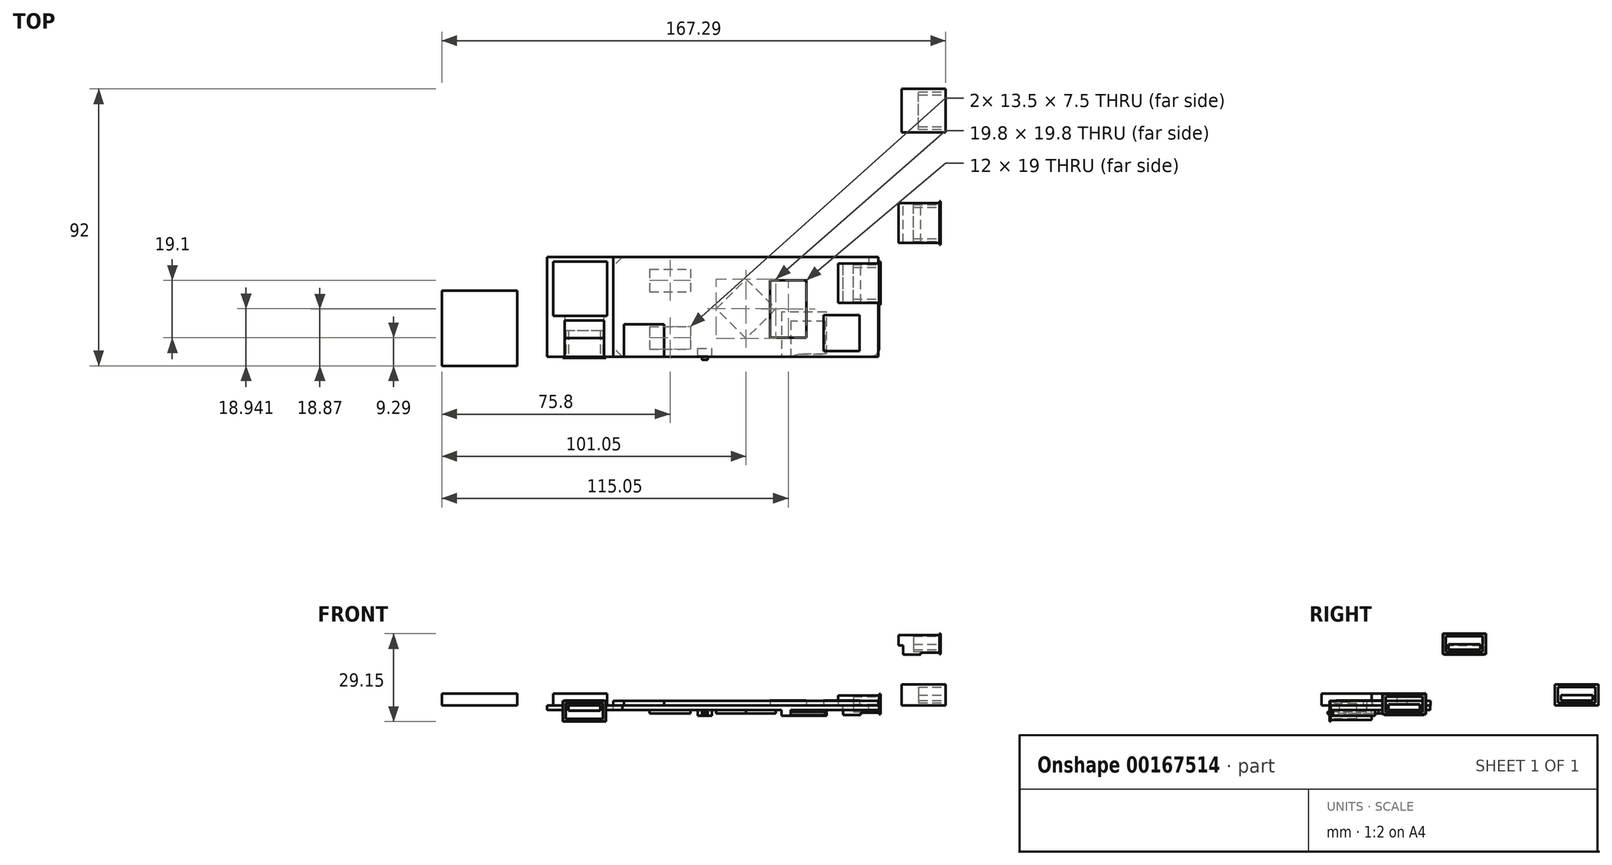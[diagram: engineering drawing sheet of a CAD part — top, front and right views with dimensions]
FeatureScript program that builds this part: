
annotation { "Feature Type Name" : "Feature", "Feature Type Description" : "" }
export const myFeature = defineFeature(function(context is Context, id is Id, definition is map)
    precondition{}
    {
        {
            var Q0;
            Q0=qCreatedBy(makeId("Top.planeOp"),FACE);
            var sketch = newSketch(context, id + "F0", { "sketchPlane" : qUnion([Q0])});
            skLineSegment(sketch, "E0", {"start": v(0, 0) * mm, "end": v(88.3, 0) * mm, "construction": true});
            skLineSegment(sketch, "E1", {"start": v(0, 0) * mm, "end": v(0, 13.55) * mm});
            skLineSegment(sketch, "E2", {"start": v(3, 16.55) * mm, "end": v(84.8, 16.55) * mm});
            skLineSegment(sketch, "E3", {"start": v(88.3, 1.25) * mm, "end": v(88.3, 0) * mm});
            skLineSegment(sketch, "E4", {"start": v(3, 16.55) * mm, "end": v(0, 13.55) * mm});
            skLineSegment(sketch, "E5.0.MirrorCS", {"start": v(0, 0) * mm, "end": v(0, -13.55) * mm});
            skLineSegment(sketch, "E6.0.MirrorCS", {"start": v(3, -16.55) * mm, "end": v(0, -13.55) * mm});
            skLineSegment(sketch, "E7.0.MirrorCS", {"start": v(3, -16.55) * mm, "end": v(85.3, -16.55) * mm});
            skArc(sketch, "E8.0.MirrorCS", {"start": v(88.3, -13.55) * mm, "mid": v(87.42, -15.67) * mm, "end": v(85.3, -16.55) * mm});
            skLineSegment(sketch, "E9.0.MirrorCS", {"start": v(88.3, -13.55) * mm, "end": v(88.3, 0) * mm});
            skLineSegment(sketch, "E10", {"start": v(84.8, 16.55) * mm, "end": v(84.8, 14.45) * mm});
            skLineSegment(sketch, "E11", {"start": v(84.8, 14.45) * mm, "end": v(76.2, 14.45) * mm});
            skLineSegment(sketch, "E12", {"start": v(76.2, 14.45) * mm, "end": v(76.2, 1.25) * mm});
            skLineSegment(sketch, "E13", {"start": v(76.2, 1.25) * mm, "end": v(88.3, 1.25) * mm});
            skLineSegment(sketch, "E14.bottom", {"start": v(52.1, 8.78) * mm, "end": v(64.1, 8.78) * mm});
            skLineSegment(sketch, "E14.top", {"start": v(52.1, -10.22) * mm, "end": v(64.1, -10.22) * mm});
            skLineSegment(sketch, "E14.left", {"start": v(52.1, 8.78) * mm, "end": v(52.1, -10.22) * mm});
            skLineSegment(sketch, "E14.right", {"start": v(64.1, 8.78) * mm, "end": v(64.1, -10.22) * mm});
            skLineSegment(sketch, "E15.bottom", {"start": v(69.8, -2.75) * mm, "end": v(81.8, -2.75) * mm});
            skLineSegment(sketch, "E15.top", {"start": v(69.8, -14.75) * mm, "end": v(81.8, -14.75) * mm});
            skLineSegment(sketch, "E15.left", {"start": v(69.8, -2.75) * mm, "end": v(69.8, -14.75) * mm});
            skLineSegment(sketch, "E15.right", {"start": v(81.8, -2.75) * mm, "end": v(81.8, -14.75) * mm});
            skLineSegment(sketch, "E16.bottom", {"start": v(12.1, 12.55) * mm, "end": v(25.6, 12.55) * mm});
            skLineSegment(sketch, "E16.top", {"start": v(12.1, 5.05) * mm, "end": v(25.6, 5.05) * mm});
            skLineSegment(sketch, "E16.left", {"start": v(12.1, 12.55) * mm, "end": v(12.1, 5.05) * mm});
            skLineSegment(sketch, "E16.right", {"start": v(25.6, 12.55) * mm, "end": v(25.6, 5.05) * mm});
            skLineSegment(sketch, "E17.bottom", {"start": v(12.1, -6.55) * mm, "end": v(25.6, -6.55) * mm});
            skLineSegment(sketch, "E17.top", {"start": v(12.1, -14.05) * mm, "end": v(25.6, -14.05) * mm});
            skLineSegment(sketch, "E17.left", {"start": v(12.1, -6.55) * mm, "end": v(12.1, -14.05) * mm});
            skLineSegment(sketch, "E17.right", {"start": v(25.6, -6.55) * mm, "end": v(25.6, -14.05) * mm});
            skLineSegment(sketch, "E18", {"start": v(44.1, 9.25) * mm, "end": v(54, -0.65) * mm});
            skLineSegment(sketch, "E19", {"start": v(54, -0.65) * mm, "end": v(44.1, -10.55) * mm});
            skLineSegment(sketch, "E20", {"start": v(44.1, -10.55) * mm, "end": v(34.2, -0.65) * mm});
            skLineSegment(sketch, "E21", {"start": v(34.2, -0.65) * mm, "end": v(44.1, 9.25) * mm});
            skLineSegment(sketch, "E22.bottom", {"start": v(28, -16.25) * mm, "end": v(29.4, -16.25) * mm});
            skLineSegment(sketch, "E22.top", {"start": v(28, -13.75) * mm, "end": v(32.7, -13.75) * mm});
            skLineSegment(sketch, "E22.left", {"start": v(28, -16.25) * mm, "end": v(28, -13.75) * mm});
            skLineSegment(sketch, "E22.right", {"start": v(32.7, -16.25) * mm, "end": v(32.7, -13.75) * mm});
            skLineSegment(sketch, "E23", {"start": v(31.3, -16.25) * mm, "end": v(31.3, -17.55) * mm});
            skLineSegment(sketch, "E24", {"start": v(31.3, -17.55) * mm, "end": v(29.4, -17.55) * mm});
            skLineSegment(sketch, "E25", {"start": v(29.4, -17.55) * mm, "end": v(29.4, -16.25) * mm});
            skLineSegment(sketch, "E26.trimOffspring", {"start": v(31.3, -16.25) * mm, "end": v(32.7, -16.25) * mm});
            skLineSegment(sketch, "E27", {"start": v(29.4, -16.25) * mm, "end": v(31.3, -16.25) * mm});
            skLineSegment(sketch, "E28", {"start": v(70.8, -1.75) * mm, "end": v(55.9, -1.75) * mm});
            skLineSegment(sketch, "E29", {"start": v(55.9, -1.75) * mm, "end": v(55.9, -16.55) * mm});
            skLineSegment(sketch, "E30", {"start": v(55.9, -16.55) * mm, "end": v(58.9, -16.55) * mm});
            skLineSegment(sketch, "E31", {"start": v(58.9, -16.55) * mm, "end": v(61.8, -15.75) * mm});
            skLineSegment(sketch, "E32", {"start": v(61.8, -15.75) * mm, "end": v(70.8, -15.75) * mm});
            skLineSegment(sketch, "E33", {"start": v(70.8, -15.75) * mm, "end": v(70.8, -1.75) * mm});
            skSolve(sketch);
        }
        {
            var Q0;
            Q0=qCreatedBy(makeId("Top.planeOp"),FACE);
            var sketch = newSketch(context, id + "F1", { "sketchPlane" : qUnion([Q0])});
            skLineSegment(sketch, "E34", {"start": v(88.3, 1.25) * mm, "end": v(76.3, 1.25) * mm});
            skLineSegment(sketch, "E35", {"start": v(76.3, 1.25) * mm, "end": v(76.3, 14.45) * mm});
            skLineSegment(sketch, "E36", {"start": v(76.3, 14.45) * mm, "end": v(88.3, 14.45) * mm});
            skLineSegment(sketch, "E37", {"start": v(88.3, 14.45) * mm, "end": v(88.3, 1.25) * mm});
            skLineSegment(sketch, "E38", {"start": v(88.3, 14.45) * mm, "end": v(88.3, 15.05) * mm});
            skLineSegment(sketch, "E39", {"start": v(88.3, 15.05) * mm, "end": v(88.7, 15.05) * mm});
            skLineSegment(sketch, "E40", {"start": v(88.7, 15.05) * mm, "end": v(88.7, 0.65) * mm});
            skLineSegment(sketch, "E41", {"start": v(88.7, 0.65) * mm, "end": v(88.3, 0.65) * mm});
            skLineSegment(sketch, "E42", {"start": v(88.3, 0.65) * mm, "end": v(88.3, 1.25) * mm});
            skLineSegment(sketch, "E43", {"start": v(76.3, 14.45) * mm, "end": v(74.7, 14.45) * mm});
            skLineSegment(sketch, "E44", {"start": v(74.7, 14.45) * mm, "end": v(74.7, 1.25) * mm});
            skLineSegment(sketch, "E45", {"start": v(74.7, 1.25) * mm, "end": v(76.3, 1.25) * mm});
            skLineSegment(sketch, "E46", {"start": v(82.1, 1.25) * mm, "end": v(82.1, 14.45) * mm});
            skSolve(sketch);
        }
        {
            var Q0;
            Q0=makeQuery(id+"F1.imprint","IMPRINT",FACE,{"disambiguationData":[TD([[makeQuery(id+"F1.imprint","IMPRINT",EDGE,{"derivedFrom":sQuery(id+"F1.wireOp",EDGE,"E34")}),-1.0]])]});
            var Q1;
            Q1=makeQuery(id+"F1.imprint","IMPRINT",FACE,{"disambiguationData":[TD([[makeQuery(id+"F1.imprint","IMPRINT",EDGE,{"derivedFrom":sQuery(id+"F1.wireOp",EDGE,"E35")}),1.0]])]});
            extrude(context, id + "F2", {"entities" : qUnion([Q0, Q1]), "depth" : (4.8 - 1.45) * mm});
        }
        {
            var Q0;
            {var subQ2=sQuery(id+"F1.wireOp",EDGE,"E35");Q0=makeQuery(id+"F1.imprint","IMPRINT",FACE,{"disambiguationData":[TD([[makeQuery(id+"F1.imprint","IMPRINT",EDGE,{"derivedFrom":subQ2}),-1.0]])]});}
            extrude(context, id + "F3", {"entities" : qUnion([Q0]), "operationType" : NewBodyOperationType.ADD, "oppositeDirection" : true, "depth" : (6.5 - 4.8 + 1.45) * mm});
        }
        {
            var Q0;
            {var subQ1=sQuery(id+"F1.wireOp",EDGE,"E37");Q0=makeQuery(id+"F1.imprint","IMPRINT",FACE,{"disambiguationData":[TD([[makeQuery(id+"F1.imprint","IMPRINT",EDGE,{"derivedFrom":subQ1}),-1.0]])]});}
            extrude(context, id + "F4", {"entities" : qUnion([Q0]), "operationType" : NewBodyOperationType.ADD, "oppositeDirection" : true, "depth" : 2.45 * mm});
        }
        {
            var Q0;
            Q0=makeQuery(id+"F1.imprint","IMPRINT",FACE,{"disambiguationData":[TD([[makeQuery(id+"F1.imprint","IMPRINT",EDGE,{"derivedFrom":sQuery(id+"F1.wireOp",EDGE,"E37")}),1.0]])]});
            extrude(context, id + "F5", {"entities" : qUnion([Q0]), "operationType" : NewBodyOperationType.ADD, "depth" : 3.85 * mm, "hasSecondDirection" : true, "secondDirectionOppositeDirection" : true, "secondDirectionDepth" : 2.95 * mm});
        }
        {
            var Q0;
            Q0=makeQuery(id+"F5.opExtrude","SWEPT_FACE",FACE,{"disambiguationData":[OSD([sQuery(id+"F1.wireOp",EDGE,"E40")])]});
            var sketch = newSketch(context, id + "F6", { "sketchPlane" : qUnion([Q0])});
            skLineSegment(sketch, "E47.bottom", {"start": v(1.75, 3) * mm, "end": v(13.95, 3) * mm});
            skLineSegment(sketch, "E47.top", {"start": v(1.75, -2.1) * mm, "end": v(13.95, -2.1) * mm});
            skLineSegment(sketch, "E47.left", {"start": v(1.75, 3) * mm, "end": v(1.75, -2.1) * mm});
            skLineSegment(sketch, "E47.right", {"start": v(13.95, 3) * mm, "end": v(13.95, -2.1) * mm});
            skLineSegment(sketch, "E48.bottom", {"start": v(2.6, 0.35) * mm, "end": v(13.1, 0.35) * mm});
            skLineSegment(sketch, "E48.top", {"start": v(2.6, -1.45) * mm, "end": v(13.1, -1.45) * mm});
            skLineSegment(sketch, "E48.left", {"start": v(2.6, 0.35) * mm, "end": v(2.6, -1.45) * mm});
            skLineSegment(sketch, "E48.right", {"start": v(13.1, 0.35) * mm, "end": v(13.1, -1.45) * mm});
            skSolve(sketch);
        }
        {
            var Q0;
            Q0=makeQuery(id+"F6.imprint","IMPRINT",FACE,{"disambiguationData":[TD([[makeQuery(id+"F6.imprint","IMPRINT",EDGE,{"derivedFrom":sQuery(id+"F6.wireOp",EDGE,"E47.bottom")}),-1.0]])]});
            extrude(context, id + "F7", {"entities" : qUnion([Q0]), "operationType" : NewBodyOperationType.REMOVE, "oppositeDirection" : true, "depth" : 9 * mm});
        }
        {
            var Q0;
            Q0=makeQuery(id+"F0.imprint","IMPRINT",FACE,{"disambiguationData":[TD([[makeQuery(id+"F0.imprint","IMPRINT",EDGE,{"derivedFrom":sQuery(id+"F0.wireOp",EDGE,"E1")}),-1.0]])]});
            var Q1;
            Q1=makeQuery(id+"F0.imprint","IMPRINT",FACE,{"disambiguationData":[TD([[makeQuery(id+"F0.imprint","IMPRINT",EDGE,{"derivedFrom":sQuery(id+"F0.wireOp",EDGE,"E14.bottom")}),-1.0]])]});
            var Q2;
            Q2=makeQuery(id+"F0.imprint","IMPRINT",FACE,{"disambiguationData":[TD([[makeQuery(id+"F0.imprint","IMPRINT",EDGE,{"derivedFrom":sQuery(id+"F0.wireOp",EDGE,"E15.bottom")}),-1.0]])]});
            var Q3;
            {var subQ1=sQuery(id+"F0.wireOp",EDGE,"E20");Q3=makeQuery(id+"F0.imprint","IMPRINT",FACE,{"disambiguationData":[TD([[makeQuery(id+"F0.imprint","IMPRINT",EDGE,{"derivedFrom":subQ1}),-1.0]])]});}
            var Q4;
            {var subQ1=sQuery(id+"F0.wireOp",EDGE,"E14.left");var subQ3=sQuery(id+"F0.wireOp",EDGE,"E18");var subQ5=makeQuery(id+"F0.imprint","INTERSECT",VERTEX,{"derivedFrom":[subQ1,subQ3]});Q4=makeQuery(id+"F0.imprint","IMPRINT",FACE,{"disambiguationData":[TD([[makeQuery(id+"F0.imprint","IMPRINT",EDGE,{"disambiguationData":[TD([[subQ5,-1.0]])],"derivedFrom":subQ1}),1.0]])]});}
            var Q5;
            Q5=makeQuery(id+"F0.imprint","IMPRINT",FACE,{"disambiguationData":[TD([[makeQuery(id+"F0.imprint","IMPRINT",EDGE,{"derivedFrom":sQuery(id+"F0.wireOp",EDGE,"E17.bottom")}),-1.0]])]});
            var Q6;
            Q6=makeQuery(id+"F0.imprint","IMPRINT",FACE,{"disambiguationData":[TD([[makeQuery(id+"F0.imprint","IMPRINT",EDGE,{"derivedFrom":sQuery(id+"F0.wireOp",EDGE,"E16.bottom")}),-1.0]])]});
            var Q7;
            {var subQ3=sQuery(id+"F0.wireOp",EDGE,"E22.bottom");Q7=makeQuery(id+"F0.imprint","IMPRINT",FACE,{"disambiguationData":[TD([[makeQuery(id+"F0.imprint","IMPRINT",EDGE,{"derivedFrom":subQ3}),1.0]])]});}
            var Q8;
            {var subQ0=sQuery(id+"F0.wireOp",EDGE,"E27");Q8=makeQuery(id+"F0.imprint","IMPRINT",FACE,{"disambiguationData":[TD([[makeQuery(id+"F0.imprint","IMPRINT",EDGE,{"derivedFrom":subQ0}),-1.0]])]});}
            var Q9;
            {var subQ14=sQuery(id+"F0.wireOp",EDGE,"E15.left");Q9=makeQuery(id+"F0.imprint","IMPRINT",FACE,{"disambiguationData":[TD([[makeQuery(id+"F0.imprint","IMPRINT",EDGE,{"derivedFrom":subQ14}),-1.0]])]});}
            var Q10;
            {var subQ1=sQuery(id+"F0.wireOp",EDGE,"E14.top");var subQ5=sQuery(id+"F0.wireOp",EDGE,"E14.right");var subQ7=makeQuery(id+"F0.imprint","INTERSECT",VERTEX,{"derivedFrom":[subQ1,subQ5]});Q10=makeQuery(id+"F0.imprint","IMPRINT",FACE,{"disambiguationData":[TD([[makeQuery(id+"F0.imprint","IMPRINT",EDGE,{"disambiguationData":[TD([[subQ7,1.0]])],"derivedFrom":subQ1}),1.0]])]});}
            extrude(context, id + "F8", {"entities" : qUnion([Q0, Q1, Q2, Q3, Q4, Q5, Q6, Q7, Q8, Q9, Q10]), "oppositeDirection" : true, "depth" : 1.45 * mm});
        }
        {
            var Q0;
            Q0=makeQuery(id+"F0.imprint","IMPRINT",FACE,{"disambiguationData":[TD([[makeQuery(id+"F0.imprint","IMPRINT",EDGE,{"derivedFrom":sQuery(id+"F0.wireOp",EDGE,"E14.bottom")}),-1.0]])]});
            var Q1;
            Q1=makeQuery(id+"F0.imprint","IMPRINT",FACE,{"disambiguationData":[TD([[makeQuery(id+"F0.imprint","IMPRINT",EDGE,{"derivedFrom":sQuery(id+"F0.wireOp",EDGE,"E15.bottom")}),-1.0]])]});
            var Q2;
            {var subQ1=sQuery(id+"F0.wireOp",EDGE,"E14.left");var subQ3=sQuery(id+"F0.wireOp",EDGE,"E18");var subQ5=makeQuery(id+"F0.imprint","INTERSECT",VERTEX,{"derivedFrom":[subQ1,subQ3]});Q2=makeQuery(id+"F0.imprint","IMPRINT",FACE,{"disambiguationData":[TD([[makeQuery(id+"F0.imprint","IMPRINT",EDGE,{"disambiguationData":[TD([[subQ5,-1.0]])],"derivedFrom":subQ1}),1.0]])]});}
            var Q3;
            {var subQ1=sQuery(id+"F0.wireOp",EDGE,"E14.top");var subQ5=sQuery(id+"F0.wireOp",EDGE,"E14.right");var subQ7=makeQuery(id+"F0.imprint","INTERSECT",VERTEX,{"derivedFrom":[subQ1,subQ5]});Q3=makeQuery(id+"F0.imprint","IMPRINT",FACE,{"disambiguationData":[TD([[makeQuery(id+"F0.imprint","IMPRINT",EDGE,{"disambiguationData":[TD([[subQ7,1.0]])],"derivedFrom":subQ1}),1.0]])]});}
            extrude(context, id + "F9", {"entities" : qUnion([Q0, Q1, Q2, Q3]), "operationType" : NewBodyOperationType.ADD, "depth" : 1.7 * mm});
        }
        {
            var Q0;
            {var subQ1=sQuery(id+"F0.wireOp",EDGE,"E20");Q0=makeQuery(id+"F0.imprint","IMPRINT",FACE,{"disambiguationData":[TD([[makeQuery(id+"F0.imprint","IMPRINT",EDGE,{"derivedFrom":subQ1}),-1.0]])]});}
            var Q1;
            {var subQ1=sQuery(id+"F0.wireOp",EDGE,"E14.left");var subQ3=sQuery(id+"F0.wireOp",EDGE,"E18");var subQ5=makeQuery(id+"F0.imprint","INTERSECT",VERTEX,{"derivedFrom":[subQ1,subQ3]});Q1=makeQuery(id+"F0.imprint","IMPRINT",FACE,{"disambiguationData":[TD([[makeQuery(id+"F0.imprint","IMPRINT",EDGE,{"disambiguationData":[TD([[subQ5,-1.0]])],"derivedFrom":subQ1}),1.0]])]});}
            var Q2;
            Q2=makeQuery(id+"F0.imprint","IMPRINT",FACE,{"disambiguationData":[TD([[makeQuery(id+"F0.imprint","IMPRINT",EDGE,{"derivedFrom":sQuery(id+"F0.wireOp",EDGE,"E16.bottom")}),-1.0]])]});
            var Q3;
            Q3=makeQuery(id+"F0.imprint","IMPRINT",FACE,{"disambiguationData":[TD([[makeQuery(id+"F0.imprint","IMPRINT",EDGE,{"derivedFrom":sQuery(id+"F0.wireOp",EDGE,"E17.bottom")}),-1.0]])]});
            extrude(context, id + "F10", {"entities" : qUnion([Q0, Q1, Q2, Q3]), "operationType" : NewBodyOperationType.ADD, "oppositeDirection" : true, "depth" : (1.45 + 1.15) * mm});
        }
        {
            var Q0;
            {var subQ3=sQuery(id+"F0.wireOp",EDGE,"E22.bottom");Q0=makeQuery(id+"F0.imprint","IMPRINT",FACE,{"disambiguationData":[TD([[makeQuery(id+"F0.imprint","IMPRINT",EDGE,{"derivedFrom":subQ3}),1.0]])]});}
            extrude(context, id + "F11", {"entities" : qUnion([Q0]), "operationType" : NewBodyOperationType.ADD, "oppositeDirection" : true, "depth" : 3.35 * mm});
        }
        {
            var Q0;
            {var subQ0=sQuery(id+"F0.wireOp",EDGE,"E27");Q0=makeQuery(id+"F0.imprint","IMPRINT",FACE,{"disambiguationData":[TD([[makeQuery(id+"F0.imprint","IMPRINT",EDGE,{"derivedFrom":subQ0}),-1.0]])]});}
            var Q1;
            {var subQ3=sQuery(id+"F0.wireOp",EDGE,"E24");Q1=makeQuery(id+"F0.imprint","IMPRINT",FACE,{"disambiguationData":[TD([[makeQuery(id+"F0.imprint","IMPRINT",EDGE,{"derivedFrom":subQ3}),-1.0]])]});}
            extrude(context, id + "F12", {"entities" : qUnion([Q0, Q1]), "operationType" : NewBodyOperationType.ADD, "oppositeDirection" : true, "depth" : 2.85 * mm, "hasSecondDirection" : true, "secondDirectionOppositeDirection" : true, "secondDirectionDepth" : 1.95 * mm});
        }
        {
            var Q0;
            {var subQ14=sQuery(id+"F0.wireOp",EDGE,"E15.left");Q0=makeQuery(id+"F0.imprint","IMPRINT",FACE,{"disambiguationData":[TD([[makeQuery(id+"F0.imprint","IMPRINT",EDGE,{"derivedFrom":subQ14}),-1.0]])]});}
            var Q1;
            {var subQ1=sQuery(id+"F0.wireOp",EDGE,"E14.top");var subQ5=sQuery(id+"F0.wireOp",EDGE,"E14.right");var subQ7=makeQuery(id+"F0.imprint","INTERSECT",VERTEX,{"derivedFrom":[subQ1,subQ5]});Q1=makeQuery(id+"F0.imprint","IMPRINT",FACE,{"disambiguationData":[TD([[makeQuery(id+"F0.imprint","IMPRINT",EDGE,{"disambiguationData":[TD([[subQ7,1.0]])],"derivedFrom":subQ1}),1.0]])]});}
            var Q2;
            {var subQ5=sQuery(id+"F0.wireOp",EDGE,"E15.left");Q2=makeQuery(id+"F0.imprint","IMPRINT",FACE,{"disambiguationData":[TD([[makeQuery(id+"F0.imprint","IMPRINT",EDGE,{"derivedFrom":subQ5}),1.0]])]});}
            extrude(context, id + "F13", {"entities" : qUnion([Q0, Q1, Q2]), "operationType" : NewBodyOperationType.ADD, "oppositeDirection" : true, "depth" : 3.45 * mm, "hasSecondDirection" : true, "secondDirectionOppositeDirection" : true, "secondDirectionDepth" : 1.45 * mm});
        }
        {
            var Q0;
            Q0=makeQuery(id+"F13.opExtrude","SWEPT_FACE",FACE,{"disambiguationData":[OSD([sQuery(id+"F0.wireOp",EDGE,"E32")])]});
            var sketch = newSketch(context, id + "F14", { "sketchPlane" : qUnion([Q0])});
            skLineSegment(sketch, "E49.bottom", {"start": v(70.4, -3.15) * mm, "end": v(58.9, -3.15) * mm});
            skLineSegment(sketch, "E49.top", {"start": v(70.4, -2.15) * mm, "end": v(58.9, -2.15) * mm});
            skLineSegment(sketch, "E49.left", {"start": v(70.4, -3.15) * mm, "end": v(70.4, -2.15) * mm});
            skLineSegment(sketch, "E49.right", {"start": v(58.9, -3.15) * mm, "end": v(58.9, -2.15) * mm});
            skSolve(sketch);
        }
        {
            var Q0;
            {var subQ5=sQuery(id+"F14.wireOp",EDGE,"E49.left");Q0=makeQuery(id+"F14.imprint","IMPRINT",FACE,{"disambiguationData":[TD([[makeQuery(id+"F14.imprint","IMPRINT",EDGE,{"derivedFrom":subQ5}),1.0]])]});}
            var Q1;
            {var subQ5=sQuery(id+"F14.wireOp",EDGE,"E49.right");Q1=makeQuery(id+"F14.imprint","IMPRINT",FACE,{"disambiguationData":[TD([[makeQuery(id+"F14.imprint","IMPRINT",EDGE,{"derivedFrom":subQ5}),-1.0]])]});}
            extrude(context, id + "F15", {"entities" : qUnion([Q0, Q1]), "operationType" : NewBodyOperationType.REMOVE, "oppositeDirection" : true, "depth" : 11 * mm, "hasSecondDirection" : true, "secondDirectionOppositeDirection" : false, "secondDirectionDepth" : 1 * mm});
        }
        {
            var Q0;
            Q0=makeQuery(id+"F2.opExtrude","SWEPT_BODY",BODY,{"disambiguationData":[OSD([sQuery(id+"F1.wireOp",EDGE,"E34"),sQuery(id+"F1.wireOp",EDGE,"E36"),sQuery(id+"F1.wireOp",EDGE,"E37"),sQuery(id+"F1.wireOp",EDGE,"E43"),sQuery(id+"F1.wireOp",EDGE,"E44"),sQuery(id+"F1.wireOp",EDGE,"E45")])]});
            var Q1;
            Q1=makeQuery(id+"F5.opExtrude","SWEPT_EDGE",EDGE,{"disambiguationData":[OSD([sQuery(id+"F1.wireOp",EDGE,"E40"),sQuery(id+"F1.wireOp",EDGE,"E41")])]});
            transform(context, id + "F16", {"entities" : qUnion([Q0]), "transformType" : TransformType.ROTATION, "transformAxis" : qUnion([Q1]), "angle" : 90 * degree, "makeCopy" : true});
        }
        {
            var Q0;
            Q0=makeQuery(id+"F16.opPattern","COPY",BODY,{"derivedFrom":makeQuery(id+"F2.opExtrude","SWEPT_BODY",BODY,{"disambiguationData":[OSD([sQuery(id+"F1.wireOp",EDGE,"E34"),sQuery(id+"F1.wireOp",EDGE,"E36"),sQuery(id+"F1.wireOp",EDGE,"E37"),sQuery(id+"F1.wireOp",EDGE,"E43"),sQuery(id+"F1.wireOp",EDGE,"E44"),sQuery(id+"F1.wireOp",EDGE,"E45")])]}),"instanceName":"1"});
            var Q1;
            {var subQ0=sQuery(id+"F1.wireOp",EDGE,"E34");var subQ1=sQuery(id+"F1.wireOp",EDGE,"E45");var subQ2=sQuery(id+"F1.wireOp",EDGE,"E44");Q1=makeQuery(id+"F16.opPattern","COPY",EDGE,{"derivedFrom":makeQuery(id+"F3.boolean.opBoolean","SPLIT",EDGE,{"disambiguationData":[TD([makeQuery(id+"F2.opExtrude","SWEPT_FACE",FACE,{"disambiguationData":[OSD([subQ2])]})])],"derivedFrom":makeQuery(id+"F2.opExtrude","CAP_EDGE",EDGE,{"disambiguationData":[OSD([subQ0,subQ1])],"isStart":true})}),"instanceName":"1"});}
            transform(context, id + "F17", {"entities" : qUnion([Q0]), "transformType" : TransformType.ROTATION, "transformAxis" : qUnion([Q1]), "angle" : 180 * degree, "makeCopy" : false});
        }
        {
            var Q0;
            Q0=makeQuery(id+"F16.opPattern","COPY",BODY,{"derivedFrom":makeQuery(id+"F2.opExtrude","SWEPT_BODY",BODY,{"disambiguationData":[OSD([sQuery(id+"F1.wireOp",EDGE,"E34"),sQuery(id+"F1.wireOp",EDGE,"E36"),sQuery(id+"F1.wireOp",EDGE,"E37"),sQuery(id+"F1.wireOp",EDGE,"E43"),sQuery(id+"F1.wireOp",EDGE,"E44"),sQuery(id+"F1.wireOp",EDGE,"E45")])]}),"instanceName":"1"});
            transform(context, id + "F18", {"entities" : qUnion([Q0]), "transformType" : TransformType.TRANSLATION_3D, "dx" : -92.3 * mm, "dy" : -17.6 * mm, "dz" : -1.45 * mm, "makeCopy" : false});
        }
        {
            var Q0;
            Q0=qCreatedBy(makeId("Top.planeOp"),FACE);
            var sketch = newSketch(context, id + "F19", { "sketchPlane" : qUnion([Q0])});
            skLineSegment(sketch, "E50.0", {"start": v(3, 16.55) * mm, "end": v(0, 13.55) * mm});
            skLineSegment(sketch, "E51.0", {"start": v(3, -16.55) * mm, "end": v(0, -13.55) * mm});
            skLineSegment(sketch, "E52", {"start": v(3, 16.55) * mm, "end": v(-22, 16.55) * mm});
            skLineSegment(sketch, "E53", {"start": v(-22, 16.55) * mm, "end": v(-22, -16.55) * mm});
            skLineSegment(sketch, "E54", {"start": v(-22, -16.55) * mm, "end": v(-16.2, -16.55) * mm});
            skLineSegment(sketch, "E55", {"start": v(0, -13.55) * mm, "end": v(0, 13.55) * mm});
            skLineSegment(sketch, "E56.0", {"start": v(-16.2, -10.35) * mm, "end": v(-16.2, -16.55) * mm});
            skLineSegment(sketch, "E57.0", {"start": v(-3, -16.55) * mm, "end": v(-3, -10.35) * mm});
            skLineSegment(sketch, "E58", {"start": v(-16.2, -10.35) * mm, "end": v(-16.2, -4.55) * mm});
            skLineSegment(sketch, "E59", {"start": v(-3, -4.55) * mm, "end": v(-3, -10.35) * mm});
            skLineSegment(sketch, "E60.0", {"start": v(-3, -4.55) * mm, "end": v(-16.2, -4.55) * mm});
            skLineSegment(sketch, "E61.trimOffspring", {"start": v(-3, -16.55) * mm, "end": v(3, -16.55) * mm});
            skLineSegment(sketch, "E62.bottom", {"start": v(-20, 15.05) * mm, "end": v(-2, 15.05) * mm});
            skLineSegment(sketch, "E62.top", {"start": v(-20, -2.95) * mm, "end": v(-2, -2.95) * mm});
            skLineSegment(sketch, "E62.left", {"start": v(-20, 15.05) * mm, "end": v(-20, -2.95) * mm});
            skLineSegment(sketch, "E62.right", {"start": v(-2, 15.05) * mm, "end": v(-2, -2.95) * mm});
            skSolve(sketch);
        }
        {
            var Q0;
            Q0=makeQuery(id+"F19.imprint","IMPRINT",FACE,{"disambiguationData":[TD([[makeQuery(id+"F19.imprint","IMPRINT",EDGE,{"derivedFrom":sQuery(id+"F19.wireOp",EDGE,"E50.0")}),-1.0]])]});
            var Q1;
            Q1=makeQuery(id+"F19.imprint","IMPRINT",FACE,{"disambiguationData":[TD([[makeQuery(id+"F19.imprint","IMPRINT",EDGE,{"derivedFrom":sQuery(id+"F19.wireOp",EDGE,"E62.bottom")}),-1.0]])]});
            extrude(context, id + "F20", {"entities" : qUnion([Q0, Q1]), "oppositeDirection" : true, "depth" : 1.45 * mm});
        }
        {
            var Q0;
            Q0=makeQuery(id+"F19.imprint","IMPRINT",FACE,{"disambiguationData":[TD([[makeQuery(id+"F19.imprint","IMPRINT",EDGE,{"derivedFrom":sQuery(id+"F19.wireOp",EDGE,"E62.bottom")}),-1.0]])]});
            extrude(context, id + "F21", {"entities" : qUnion([Q0]), "depth" : 4 * mm});
        }
        {
            var Q0;
            Q0=makeQuery(id+"F2.opExtrude","SWEPT_BODY",BODY,{"disambiguationData":[OSD([sQuery(id+"F1.wireOp",EDGE,"E34"),sQuery(id+"F1.wireOp",EDGE,"E36"),sQuery(id+"F1.wireOp",EDGE,"E37"),sQuery(id+"F1.wireOp",EDGE,"E43"),sQuery(id+"F1.wireOp",EDGE,"E44"),sQuery(id+"F1.wireOp",EDGE,"E45")])]});
            transform(context, id + "F22", {"entities" : qUnion([Q0]), "transformType" : TransformType.TRANSLATION_3D, "dx" : 20 * mm, "dy" : 20 * mm, "dz" : 20 * mm, "makeCopy" : true});
        }
        {
            var Q0;
            Q0=qCreatedBy(makeId("Top.planeOp"),FACE);
            var sketch = newSketch(context, id + "F23", { "sketchPlane" : qUnion([Q0])});
            skLineSegment(sketch, "E63.bottom", {"start": v(95.79, 57.91) * mm, "end": v(110.34, 57.91) * mm});
            skLineSegment(sketch, "E63.top", {"start": v(95.79, 72.41) * mm, "end": v(110.34, 72.41) * mm});
            skLineSegment(sketch, "E63.left", {"start": v(95.79, 57.91) * mm, "end": v(95.79, 72.41) * mm});
            skLineSegment(sketch, "E63.right", {"start": v(110.34, 57.91) * mm, "end": v(110.34, 72.41) * mm});
            skSolve(sketch);
        }
        {
            var Q0;
            Q0=makeQuery(id+"F23.imprint","IMPRINT",FACE,{"disambiguationData":[TD([[makeQuery(id+"F23.imprint","IMPRINT",EDGE,{"derivedFrom":sQuery(id+"F23.wireOp",EDGE,"E63.bottom")}),1.0]])]});
            extrude(context, id + "F24", {"entities" : qUnion([Q0]), "depth" : 7 * mm});
        }
        {
            var Q0;
            Q0=makeQuery(id+"F24.opExtrude","SWEPT_FACE",FACE,{"disambiguationData":[OSD([sQuery(id+"F23.wireOp",EDGE,"E63.right")])]});
            var sketch = newSketch(context, id + "F25", { "sketchPlane" : qUnion([Q0])});
            skLineSegment(sketch, "E64.bottom", {"start": v(58.91, 6.06) * mm, "end": v(71.41, 6.06) * mm});
            skLineSegment(sketch, "E64.top", {"start": v(58.91, 0.94) * mm, "end": v(71.41, 0.94) * mm});
            skLineSegment(sketch, "E64.left", {"start": v(58.91, 6.06) * mm, "end": v(58.91, 0.94) * mm});
            skLineSegment(sketch, "E64.right", {"start": v(71.41, 6.06) * mm, "end": v(71.41, 0.94) * mm});
            skLineSegment(sketch, "E65.bottom", {"start": v(59.91, 3.5) * mm, "end": v(70.41, 3.5) * mm});
            skLineSegment(sketch, "E65.top", {"start": v(59.91, 1.7) * mm, "end": v(70.41, 1.7) * mm});
            skLineSegment(sketch, "E65.left", {"start": v(59.91, 3.5) * mm, "end": v(59.91, 1.7) * mm});
            skLineSegment(sketch, "E65.right", {"start": v(70.41, 3.5) * mm, "end": v(70.41, 1.7) * mm});
            skSolve(sketch);
        }
        {
            var Q0;
            Q0=makeQuery(id+"F25.imprint","IMPRINT",FACE,{"disambiguationData":[TD([[makeQuery(id+"F25.imprint","IMPRINT",EDGE,{"derivedFrom":sQuery(id+"F25.wireOp",EDGE,"E64.bottom")}),-1.0]])]});
            extrude(context, id + "F26", {"entities" : qUnion([Q0]), "operationType" : NewBodyOperationType.REMOVE, "oppositeDirection" : true, "depth" : 9 * mm});
        }
        {
            var Q0;
            Q0=makeQuery(id+"F8.opExtrude","SWEPT_BODY",BODY,{"disambiguationData":[OSD([sQuery(id+"F0.wireOp",EDGE,"E1"),sQuery(id+"F0.wireOp",EDGE,"E2"),sQuery(id+"F0.wireOp",EDGE,"E3"),sQuery(id+"F0.wireOp",EDGE,"E4"),sQuery(id+"F0.wireOp",EDGE,"E5.0.MirrorCS"),sQuery(id+"F0.wireOp",EDGE,"E6.0.MirrorCS"),sQuery(id+"F0.wireOp",EDGE,"E7.0.MirrorCS"),sQuery(id+"F0.wireOp",EDGE,"E8.0.MirrorCS"),sQuery(id+"F0.wireOp",EDGE,"E9.0.MirrorCS"),sQuery(id+"F0.wireOp",EDGE,"E10"),sQuery(id+"F0.wireOp",EDGE,"E11"),sQuery(id+"F0.wireOp",EDGE,"E12"),sQuery(id+"F0.wireOp",EDGE,"E13"),sQuery(id+"F0.wireOp",EDGE,"E30")])]});
            transform(context, id + "F27", {"entities" : qUnion([Q0]), "transformType" : TransformType.TRANSLATION_3D, "dx" : 0 * mm, "dy" : 0 * mm, "dz" : 0 * mm, "makeCopy" : true});
        }
        {
            var Q0;
            Q0=qCreatedBy(makeId("Top.planeOp"),FACE);
            var sketch = newSketch(context, id + "F28", { "sketchPlane" : qUnion([Q0])});
            skLineSegment(sketch, "E66", {"start": v(0, 0) * mm, "end": v(0, 16.6) * mm});
            skLineSegment(sketch, "E67", {"start": v(0, 16.6) * mm, "end": v(88.05, 16.6) * mm});
            skLineSegment(sketch, "E68", {"start": v(88.05, 16.6) * mm, "end": v(88.05, -16.6) * mm});
            skLineSegment(sketch, "E69", {"start": v(88.05, -16.6) * mm, "end": v(16.91, -16.6) * mm});
            skLineSegment(sketch, "E70", {"start": v(16.91, -16.6) * mm, "end": v(16.91, -5.76) * mm});
            skLineSegment(sketch, "E71", {"start": v(16.91, -5.76) * mm, "end": v(3.5, -5.76) * mm});
            skLineSegment(sketch, "E72", {"start": v(3.5, -5.76) * mm, "end": v(3.5, -16.6) * mm});
            skLineSegment(sketch, "E73", {"start": v(3.5, -16.6) * mm, "end": v(0, -16.6) * mm});
            skLineSegment(sketch, "E74", {"start": v(0, -16.6) * mm, "end": v(0, 0) * mm});
            skLineSegment(sketch, "E75", {"start": v(0, 0) * mm, "end": v(128.01, 0) * mm, "construction": true});
            skLineSegment(sketch, "E76.bottom", {"start": v(-56.95, 5.41) * mm, "end": v(-31.95, 5.41) * mm});
            skLineSegment(sketch, "E76.top", {"start": v(-56.95, -19.59) * mm, "end": v(-31.95, -19.59) * mm});
            skLineSegment(sketch, "E76.left", {"start": v(-56.95, 5.41) * mm, "end": v(-56.95, -19.59) * mm});
            skLineSegment(sketch, "E76.right", {"start": v(-31.95, 5.41) * mm, "end": v(-31.95, -19.59) * mm});
            skLineSegment(sketch, "E77", {"start": v(-44.45, 5.41) * mm, "end": v(-44.45, -19.59) * mm, "construction": true});
            skLineSegment(sketch, "E78", {"start": v(-31.95, -7.09) * mm, "end": v(-56.95, -7.09) * mm, "construction": true});
            skCircle(sketch, "E79", {"center": v(-44.45, -7.09) * mm, "radius": 1 * mm});
            skSolve(sketch);
        }
        {
            var Q0;
            Q0=makeQuery(id+"F28.imprint","IMPRINT",FACE,{"disambiguationData":[TD([[makeQuery(id+"F28.imprint","IMPRINT",EDGE,{"derivedFrom":sQuery(id+"F28.wireOp",EDGE,"E66")}),-1.0]])]});
            extrude(context, id + "F29", {"entities" : qUnion([Q0]), "depth" : 1.5 * mm});
        }
        {
            var Q0;
            Q0=makeQuery(id+"F28.imprint","IMPRINT",FACE,{"disambiguationData":[TD([[makeQuery(id+"F28.imprint","IMPRINT",EDGE,{"derivedFrom":sQuery(id+"F28.wireOp",EDGE,"E76.bottom")}),-1.0]])]});
            extrude(context, id + "F30", {"entities" : qUnion([Q0]), "depth" : 4 * mm});
        }
        {
            var Q0;
            Q0=makeQuery(id+"F28.imprint","IMPRINT",FACE,{"disambiguationData":[TD([[makeQuery(id+"F28.imprint","IMPRINT",EDGE,{"derivedFrom":sQuery(id+"F28.wireOp",EDGE,"E79")}),1.0]])]});
            extrude(context, id + "F31", {"entities" : qUnion([Q0]), "operationType" : NewBodyOperationType.ADD, "depth" : 4 * mm});
        }
    });
